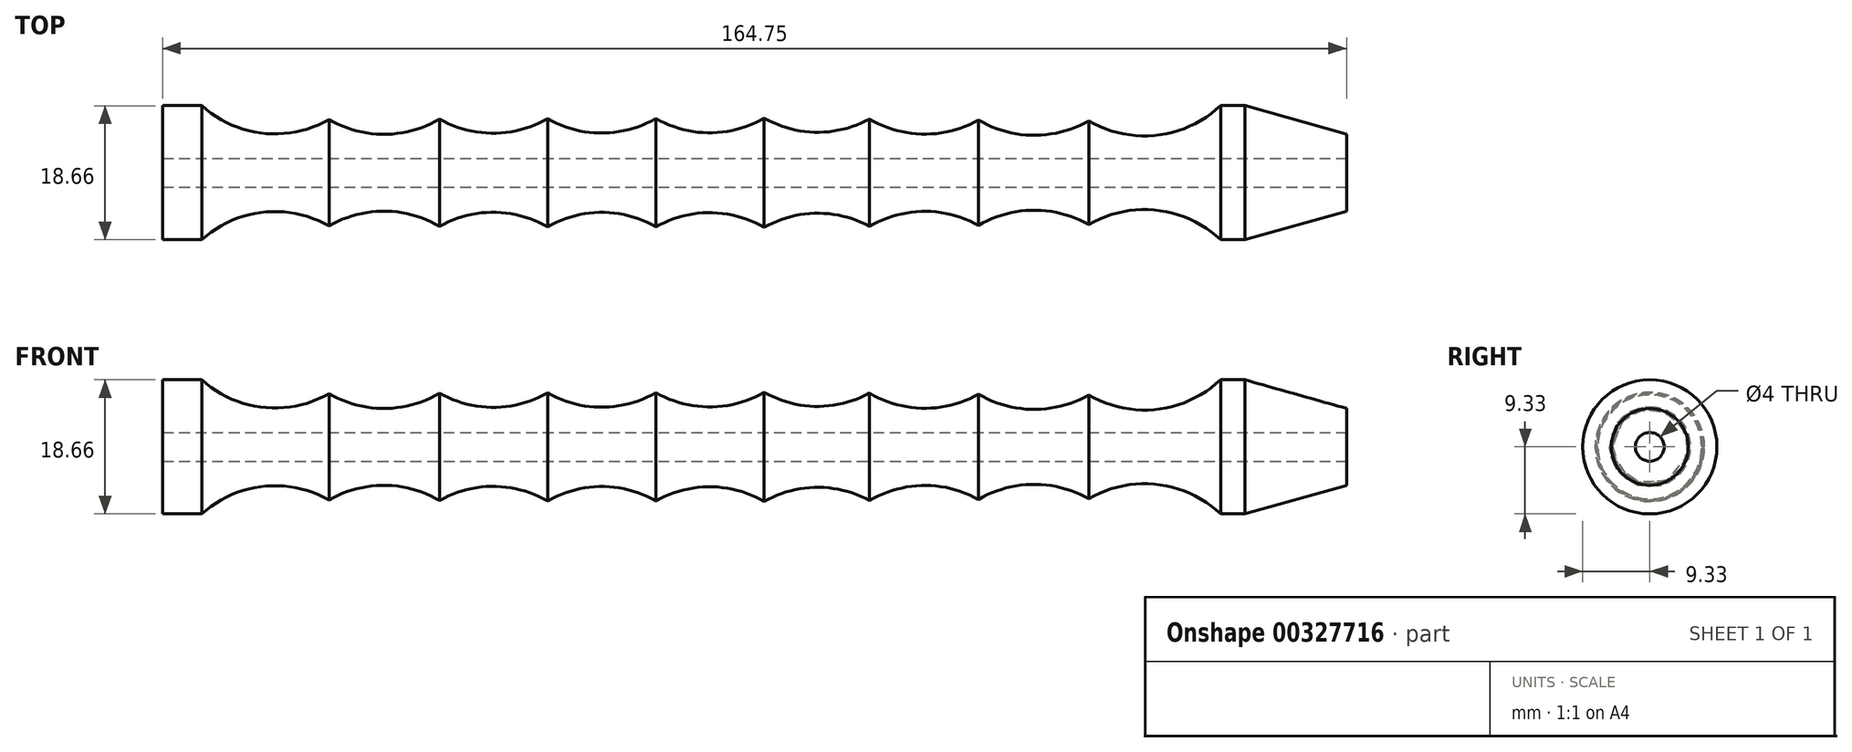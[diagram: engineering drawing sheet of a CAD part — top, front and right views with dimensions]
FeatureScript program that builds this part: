
annotation { "Feature Type Name" : "Feature", "Feature Type Description" : "" }
export const myFeature = defineFeature(function(context is Context, id is Id, definition is map)
    precondition{}
    {
        {
            var Q0;
            Q0=qCreatedBy(makeId("Front.planeOp"),FACE);
            var sketch = newSketch(context, id + "F0", { "sketchPlane" : qUnion([Q0])});
            skLineSegment(sketch, "E0", {"start": v(-75.22, 9.33) * mm, "end": v(-69.78, 9.33) * mm});
            skArc(sketch, "E1", {"start": v(-69.78, 9.33) * mm, "mid": v(-61.24, 5.5) * mm, "end": v(-52.08, 7.4) * mm});
            skArc(sketch, "E2", {"start": v(-36.68, 7.48) * mm, "mid": v(-29.16, 5.5) * mm, "end": v(-21.66, 7.53) * mm});
            skArc(sketch, "E3", {"start": v(-21.66, 7.53) * mm, "mid": v(-14.12, 5.52) * mm, "end": v(-6.58, 7.56) * mm});
            skArc(sketch, "E4", {"start": v(-6.58, 7.56) * mm, "mid": v(0.97, 5.56) * mm, "end": v(8.5, 7.61) * mm});
            skArc(sketch, "E5", {"start": v(8.5, 7.61) * mm, "mid": v(15.8, 5.63) * mm, "end": v(23.13, 7.49) * mm});
            skLineSegment(sketch, "E6.trimOffspring", {"start": v(72, 9.33) * mm, "end": v(75.4, 9.33) * mm});
            skArc(sketch, "E7.trimOffspring", {"start": v(-52.08, 7.4) * mm, "mid": v(-44.37, 5.35) * mm, "end": v(-36.68, 7.48) * mm});
            skArc(sketch, "E8.trimOffspring", {"start": v(23.13, 7.49) * mm, "mid": v(30.7, 5.37) * mm, "end": v(38.3, 7.32) * mm});
            skArc(sketch, "E9.trimOffspring", {"start": v(38.3, 7.32) * mm, "mid": v(45.97, 5.22) * mm, "end": v(53.65, 7.22) * mm});
            skArc(sketch, "E10.trimOffspring", {"start": v(53.65, 7.22) * mm, "mid": v(63.18, 5.23) * mm, "end": v(72, 9.33) * mm});
            skLineSegment(sketch, "E11", {"start": v(-75.22, 9.33) * mm, "end": v(-75.22, 0) * mm});
            skLineSegment(sketch, "E12", {"start": v(-75.22, 0) * mm, "end": v(75.22, 0) * mm});
            skLineSegment(sketch, "E13", {"start": v(75.4, 9.33) * mm, "end": v(89.53, 5.35) * mm});
            skLineSegment(sketch, "E14", {"start": v(89.53, 5.35) * mm, "end": v(89.53, 0) * mm});
            skLineSegment(sketch, "E15", {"start": v(89.53, 0) * mm, "end": v(75.4, 0) * mm});
            skLineSegment(sketch, "E16", {"start": v(75.22, 0) * mm, "end": v(75.4, 0) * mm});
            skSolve(sketch);
        }
        {
            var Q0;
            Q0=makeQuery(id+"F0.imprint","IMPRINT",FACE,{"disambiguationData":[TD([[makeQuery(id+"F0.imprint","IMPRINT",EDGE,{"derivedFrom":sQuery(id+"F0.wireOp",EDGE,"E0")}),-1.0]])]});
            var Q1;
            Q1=sQuery(id+"F0.wireOp",EDGE,"E12");
            revolve(context, id + "F1", {"entities" : qUnion([Q0]), "axis" : qUnion([Q1]), "revolveType" : RevolveType.FULL});
        }
        {
            var Q0;
            Q0=makeQuery(id+"F1.opRevolve","SWEPT_FACE",FACE,{"disambiguationData":[OSD([sQuery(id+"F0.wireOp",EDGE,"E14")])]});
            var sketch = newSketch(context, id + "F2", { "sketchPlane" : qUnion([Q0])});
            skCircle(sketch, "E17", {"center": v(0, 0) * mm, "radius": 2 * mm});
            skSolve(sketch);
        }
        {
            var Q0;
            Q0=makeQuery(id+"F2.imprint","IMPRINT",FACE,{"disambiguationData":[TD([[makeQuery(id+"F2.imprint","IMPRINT",EDGE,{"derivedFrom":sQuery(id+"F2.wireOp",EDGE,"E17")}),1.0]])]});
            extrude(context, id + "F3", {"entities" : qUnion([Q0]), "operationType" : NewBodyOperationType.REMOVE, "oppositeDirection" : true, "depth" : 165 * mm});
        }
    });
